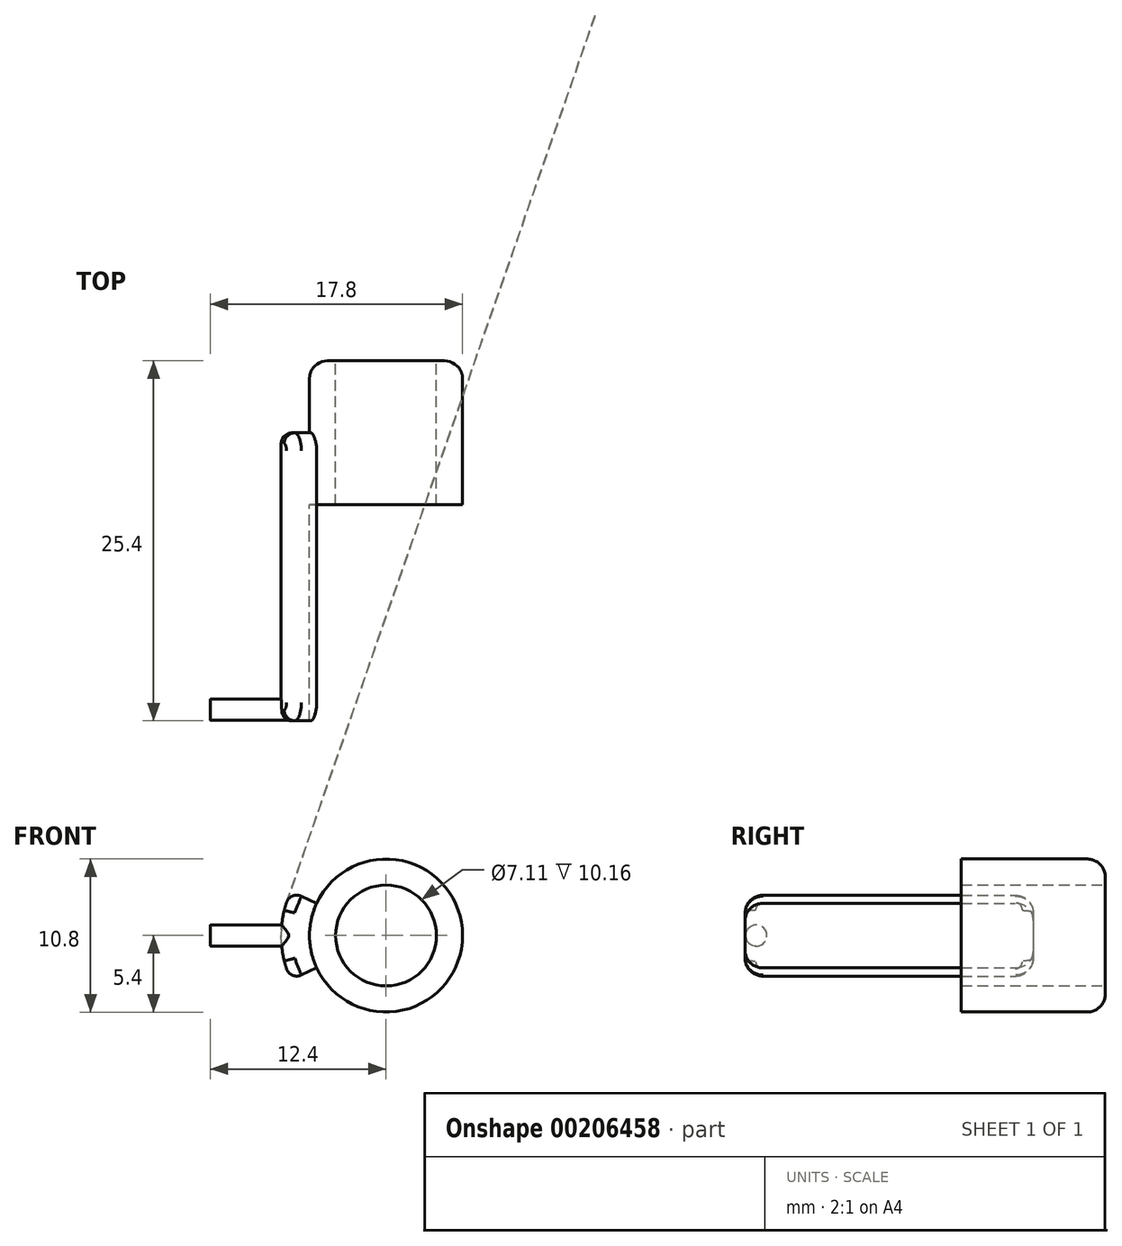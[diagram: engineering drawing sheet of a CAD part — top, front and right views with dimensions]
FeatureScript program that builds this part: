
annotation { "Feature Type Name" : "Feature", "Feature Type Description" : "" }
export const myFeature = defineFeature(function(context is Context, id is Id, definition is map)
    precondition{}
    {
        {
            var Q0;
            Q0=qCreatedBy(makeId("Front.planeOp"),FACE);
            var sketch = newSketch(context, id + "F0", { "sketchPlane" : qUnion([Q0])});
            skCircle(sketch, "E0", {"center": v(0, 0) * mm, "radius": 5.4 * mm});
            skCircle(sketch, "E1", {"center": v(0, 0) * mm, "radius": 3.56 * mm});
            skSolve(sketch);
        }
        {
            var Q0;
            Q0 = qSketchRegion(id + "F0", true);
            extrude(context, id + "F1", {"entities" : qUnion([Q0]), "depth" : 10.16 * mm});
        }
        {
            var Q0;
            Q0=qCreatedBy(makeId("Front.planeOp"),FACE);
            cPlane(context, id + "F2", {"entities" : qUnion([Q0]), "cplaneType" : CPlaneType.OFFSET, "offset" : 5.08 * mm, "width" : 152.4 * mm, "height" : 152.4 * mm});
        }
        {
            var Q0;
            Q0=qCreatedBy(id+"F2.planeOp",FACE);
            var sketch = newSketch(context, id + "F3", { "sketchPlane" : qUnion([Q0])});
            skArc(sketch, "E2", {"start": v(-4.9, 2.28) * mm, "mid": v(-5.4, 0) * mm, "end": v(-4.89, -2.29) * mm});
            skArc(sketch, "E3", {"start": v(-6.7, 3.12) * mm, "mid": v(-7.4, 0) * mm, "end": v(-6.7, -3.13) * mm});
            skLineSegment(sketch, "E4", {"start": v(-6.7, 3.12) * mm, "end": v(-4.9, 2.28) * mm});
            skLineSegment(sketch, "E5", {"start": v(-4.89, -2.29) * mm, "end": v(-6.7, -3.13) * mm});
            skSolve(sketch);
        }
        {
            var Q0;
            Q0 = qSketchRegion(id + "F3", true);
            extrude(context, id + "F4", {"entities" : qUnion([Q0]), "operationType" : NewBodyOperationType.ADD, "depth" : 20.32 * mm});
        }
        {
            var Q0;
            Q0=qCreatedBy(makeId("Right.planeOp"),FACE);
            cPlane(context, id + "F5", {"entities" : qUnion([Q0]), "cplaneType" : CPlaneType.OFFSET, "offset" : 5.4 * mm, "oppositeDirection" : true, "width" : 152.4 * mm, "height" : 152.4 * mm});
        }
        {
            var Q0;
            Q0=makeQuery(id+"F4.opExtrude","CAP_EDGE",EDGE,{"disambiguationData":[OSD([sQuery(id+"F3.wireOp",EDGE,"E5")])],"isStart":false});
            fillet(context, id + "F6", {"entities" : qUnion([Q0]), "radius" : 1.27 * mm, "tangentPropagation" : true, "allowEdgeOverflow" : false});
        }
        {
            var Q0;
            Q0=makeQuery(id+"F4.opExtrude","CAP_EDGE",EDGE,{"disambiguationData":[OSD([sQuery(id+"F3.wireOp",EDGE,"E4")])],"isStart":false});
            fillet(context, id + "F7", {"entities" : qUnion([Q0]), "radius" : 1.27 * mm, "tangentPropagation" : true, "allowEdgeOverflow" : false});
        }
        {
            var Q0;
            Q0=makeQuery(id+"F4.opExtrude","SWEPT_EDGE",EDGE,{"disambiguationData":[OSD([sQuery(id+"F3.wireOp",EDGE,"E3"),sQuery(id+"F3.wireOp",EDGE,"E5")])]});
            var Q1;
            Q1=makeQuery(id+"F4.opExtrude","CAP_EDGE",EDGE,{"disambiguationData":[OSD([sQuery(id+"F3.wireOp",EDGE,"E3")])],"isStart":true});
            fillet(context, id + "F8", {"entities" : qUnion([Q0, Q1]), "radius" : 0.76 * mm, "tangentPropagation" : true, "allowEdgeOverflow" : false});
        }
        {
            var Q0;
            Q0=makeQuery(id+"F4.opExtrude","CAP_EDGE",EDGE,{"disambiguationData":[OSD([sQuery(id+"F3.wireOp",EDGE,"E4")])],"isStart":true});
            var Q1;
            Q1=makeQuery(id+"F4.opExtrude","CAP_EDGE",EDGE,{"disambiguationData":[OSD([sQuery(id+"F3.wireOp",EDGE,"E5")])],"isStart":true});
            fillet(context, id + "F9", {"entities" : qUnion([Q0, Q1]), "radius" : 1.27 * mm, "tangentPropagation" : true, "allowEdgeOverflow" : false});
        }
        {
            var Q0;
            Q0=makeQuery(id+"F1.opExtrude","CAP_EDGE",EDGE,{"disambiguationData":[OSD([sQuery(id+"F0.wireOp",EDGE,"E0")])],"isStart":true});
            fillet(context, id + "F10", {"entities" : qUnion([Q0]), "radius" : 1.27 * mm, "tangentPropagation" : true, "allowEdgeOverflow" : false});
        }
        {
            var Q0;
            Q0=qCreatedBy(id+"F5.planeOp",FACE);
            var sketch = newSketch(context, id + "F11", { "sketchPlane" : qUnion([Q0])});
            skCircle(sketch, "E6", {"center": v(-24.62, 0) * mm, "radius": 0.75 * mm});
            skSolve(sketch);
        }
        {
            var Q0;
            Q0 = qSketchRegion(id + "F11", true);
            extrude(context, id + "F12", {"entities" : qUnion([Q0]), "operationType" : NewBodyOperationType.ADD, "oppositeDirection" : true, "depth" : 7 * mm, "offsetDistance" : 25 * mm});
        }
        {
            var Q0;
            Q0=makeQuery(id+"F12.opExtrude","CAP_EDGE",EDGE,{"disambiguationData":[OSD([sQuery(id+"F11.wireOp",EDGE,"E6")])],"isStart":false});
            fillet(context, id + "F13", {"entities" : qUnion([Q0]), "radius" : 0.05 * mm, "tangentPropagation" : true, "allowEdgeOverflow" : false});
        }
    });
